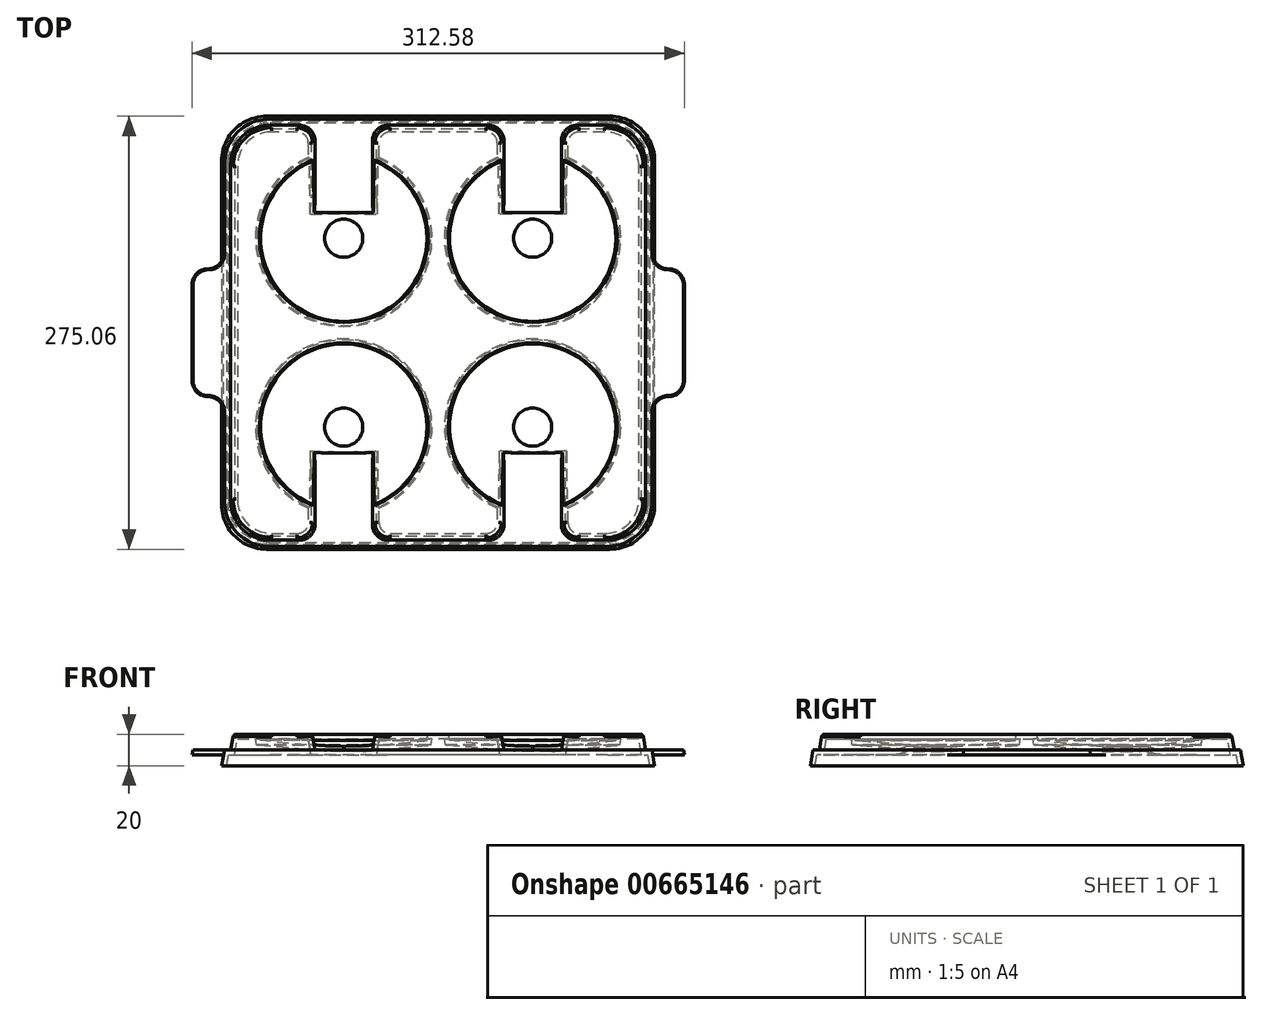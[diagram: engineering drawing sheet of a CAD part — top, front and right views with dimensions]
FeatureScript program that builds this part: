
annotation { "Feature Type Name" : "Feature", "Feature Type Description" : "" }
export const myFeature = defineFeature(function(context is Context, id is Id, definition is map)
    precondition{}
    {
        {
            var Q0;
            Q0=qCreatedBy(makeId("Top.planeOp"),FACE);
            var sketch = newSketch(context, id + "F0", { "sketchPlane" : qUnion([Q0])});
            skLineSegment(sketch, "E0", {"start": v(-60, 63.68) * mm, "end": v(-60, -68.5) * mm, "construction": true});
            skLineSegment(sketch, "E1", {"start": v(-108.87, 60) * mm, "end": v(91.95, 60) * mm, "construction": true});
            skLineSegment(sketch, "E2.MirrorCS", {"start": v(60, 63.68) * mm, "end": v(60, -68.5) * mm, "construction": true});
            skLineSegment(sketch, "E3.MirrorCS", {"start": v(-108.87, -60) * mm, "end": v(91.95, -60) * mm, "construction": true});
            skLineSegment(sketch, "E4", {"start": v(-130, 152.73) * mm, "end": v(-130, -156.18) * mm, "construction": true});
            skLineSegment(sketch, "E5", {"start": v(-201.2, -130) * mm, "end": v(310.8, -130) * mm, "construction": true});
            skLineSegment(sketch, "E6.MirrorCS", {"start": v(130, 152.73) * mm, "end": v(130, -156.18) * mm, "construction": true});
            skLineSegment(sketch, "E7.MirrorCS", {"start": v(-201.2, 130) * mm, "end": v(310.8, 130) * mm, "construction": true});
            skLineSegment(sketch, "E8.bottom", {"start": v(-130, 130) * mm, "end": v(130, 130) * mm});
            skLineSegment(sketch, "E8.top", {"start": v(-130, -130) * mm, "end": v(130, -130) * mm});
            skLineSegment(sketch, "E8.left", {"start": v(-130, 130) * mm, "end": v(-130, -130) * mm});
            skLineSegment(sketch, "E8.right", {"start": v(130, 130) * mm, "end": v(130, -130) * mm});
            skSolve(sketch);
        }
        {
            var Q0;
            Q0=makeQuery(id+"F0.imprint","IMPRINT",FACE,{"disambiguationData":[TD([[makeQuery(id+"F0.imprint","IMPRINT",EDGE,{"derivedFrom":sQuery(id+"F0.wireOp",EDGE,"E8.bottom")}),-1.0]])]});
            extrude(context, id + "F1", {"entities" : qUnion([Q0]), "oppositeDirection" : true, "depth" : 10 * mm, "offsetDistance" : 25 * mm, "hasDraft" : true, "draftAngle" : 10 * degree});
        }
        {
            var Q0;
            Q0=makeQuery(id+"F1.opExtrude","CAP_FACE",FACE,{"disambiguationData":[OSD([sQuery(id+"F0.wireOp",EDGE,"E8.bottom"),sQuery(id+"F0.wireOp",EDGE,"E8.top"),sQuery(id+"F0.wireOp",EDGE,"E8.left"),sQuery(id+"F0.wireOp",EDGE,"E8.right")])],"isStart":false});
            var sketch = newSketch(context, id + "F2", { "sketchPlane" : qUnion([Q0])});
            skLineSegment(sketch, "E9", {"start": v(-264, 135.76) * mm, "end": v(236, 135.76) * mm, "construction": true});
            skLineSegment(sketch, "E10.MirrorCS", {"start": v(-264, -135.76) * mm, "end": v(236, -135.76) * mm, "construction": true});
            skLineSegment(sketch, "E11", {"start": v(-135.76, 316.9) * mm, "end": v(-135.76, -183.1) * mm, "construction": true});
            skLineSegment(sketch, "E12.MirrorCS", {"start": v(135.76, 316.9) * mm, "end": v(135.76, -183.1) * mm, "construction": true});
            skLineSegment(sketch, "E13.bottom", {"start": v(-135.76, 135.76) * mm, "end": v(135.76, 135.76) * mm});
            skLineSegment(sketch, "E13.top", {"start": v(-135.76, -135.76) * mm, "end": v(135.76, -135.76) * mm});
            skLineSegment(sketch, "E13.left", {"start": v(-135.76, 135.76) * mm, "end": v(-135.76, -135.76) * mm});
            skLineSegment(sketch, "E13.right", {"start": v(135.76, 135.76) * mm, "end": v(135.76, -135.76) * mm});
            skSolve(sketch);
        }
        {
            var Q0;
            Q0=makeQuery(id+"F2.imprint","IMPRINT",FACE,{"disambiguationData":[TD([[makeQuery(id+"F2.imprint","IMPRINT",EDGE,{"derivedFrom":sQuery(id+"F2.wireOp",EDGE,"E13.bottom")}),-1.0]])]});
            var Q1;
            Q1=makeQuery(id+"F2.imprint","IMPRINT",FACE,{"disambiguationData":[TD([[makeQuery(id+"F2.imprint","IMPRINT",EDGE,{"derivedFrom":makeQuery(id+"F1.opExtrude","CAP_EDGE",EDGE,{"disambiguationData":[OSD([sQuery(id+"F0.wireOp",EDGE,"E8.bottom")])],"isStart":false})}),1.0]])]});
            extrude(context, id + "F3", {"entities" : qUnion([Q0, Q1]), "operationType" : NewBodyOperationType.ADD, "depth" : 10 * mm, "offsetDistance" : 25 * mm, "hasDraft" : true, "draftAngle" : 10 * degree});
        }
        {
            var Q0;
            Q0=makeQuery(id+"F1.opExtrude","CAP_FACE",FACE,{"disambiguationData":[OSD([sQuery(id+"F0.wireOp",EDGE,"E8.bottom"),sQuery(id+"F0.wireOp",EDGE,"E8.top"),sQuery(id+"F0.wireOp",EDGE,"E8.left"),sQuery(id+"F0.wireOp",EDGE,"E8.right")])],"isStart":true});
            var sketch = newSketch(context, id + "F4", { "sketchPlane" : qUnion([Q0])});
            skLineSegment(sketch, "E14", {"start": v(-130, 0) * mm, "end": v(130, 0) * mm, "construction": true});
            skLineSegment(sketch, "E15", {"start": v(-130, -60) * mm, "end": v(130, -60) * mm, "construction": true});
            skLineSegment(sketch, "E16.MirrorCS", {"start": v(-130, 60) * mm, "end": v(130, 60) * mm, "construction": true});
            skLineSegment(sketch, "E17", {"start": v(-60, -130) * mm, "end": v(-60, 130) * mm, "construction": true});
            skLineSegment(sketch, "E18", {"start": v(0, -130) * mm, "end": v(0, 130) * mm, "construction": true});
            skLineSegment(sketch, "E19.MirrorCS", {"start": v(60, -130) * mm, "end": v(60, 130) * mm, "construction": true});
            skCircle(sketch, "E20", {"center": v(-60, -60) * mm, "radius": 53.5 * mm});
            skCircle(sketch, "E21", {"center": v(-60, 60) * mm, "radius": 53.5 * mm});
            skCircle(sketch, "E22", {"center": v(60, 60) * mm, "radius": 53.5 * mm});
            skCircle(sketch, "E23", {"center": v(60, -60) * mm, "radius": 53.5 * mm});
            skCircle(sketch, "E24", {"center": v(60, 60) * mm, "radius": 25 * mm, "construction": true});
            skLineSegment(sketch, "E25", {"start": v(80, 150) * mm, "end": v(80, 75) * mm});
            skLineSegment(sketch, "E26.MirrorCS", {"start": v(40, 130) * mm, "end": v(40, 75) * mm});
            skLineSegment(sketch, "E27.MirrorCS", {"start": v(-40, 130) * mm, "end": v(-40, 75) * mm});
            skLineSegment(sketch, "E28.MirrorCS", {"start": v(-80, 130) * mm, "end": v(-80, 75) * mm});
            skCircle(sketch, "E29.MirrorC", {"center": v(-60, 60) * mm, "radius": 25 * mm, "construction": true});
            skCircle(sketch, "E30.MirrorC", {"center": v(60, -60) * mm, "radius": 25 * mm, "construction": true});
            skLineSegment(sketch, "E31.MirrorCS", {"start": v(40, -130) * mm, "end": v(40, -75) * mm});
            skLineSegment(sketch, "E32.MirrorCS", {"start": v(80, -130) * mm, "end": v(80, -75) * mm});
            skCircle(sketch, "E33.MirrorC", {"center": v(-60, -60) * mm, "radius": 25 * mm, "construction": true});
            skLineSegment(sketch, "E34.MirrorCS", {"start": v(-80, -130) * mm, "end": v(-80, -75) * mm});
            skLineSegment(sketch, "E35.MirrorCS", {"start": v(-40, -130) * mm, "end": v(-40, -75) * mm});
            skLineSegment(sketch, "E36", {"start": v(40, 75) * mm, "end": v(80, 75) * mm});
            skLineSegment(sketch, "E37.MirrorCS", {"start": v(-40, 75) * mm, "end": v(-80, 75) * mm});
            skLineSegment(sketch, "E38.MirrorCS", {"start": v(-40, -75) * mm, "end": v(-80, -75) * mm});
            skLineSegment(sketch, "E39.MirrorCS", {"start": v(40, -75) * mm, "end": v(80, -75) * mm});
            skPoint(sketch, "E40.orphan", {"position": v(80, 130) * mm});
            skLineSegment(sketch, "E41.MirrorCS", {"start": v(40, 150) * mm, "end": v(40, 75) * mm});
            skLineSegment(sketch, "E42.MirrorCS", {"start": v(-40, 150) * mm, "end": v(-40, 75) * mm});
            skLineSegment(sketch, "E43.MirrorCS", {"start": v(-80, 150) * mm, "end": v(-80, 75) * mm});
            skLineSegment(sketch, "E44.MirrorCS", {"start": v(-40, -150) * mm, "end": v(-40, -75) * mm});
            skLineSegment(sketch, "E45.MirrorCS", {"start": v(-80, -150) * mm, "end": v(-80, -75) * mm});
            skLineSegment(sketch, "E46.MirrorCS", {"start": v(40, -150) * mm, "end": v(40, -75) * mm});
            skLineSegment(sketch, "E47.MirrorCS", {"start": v(80, -150) * mm, "end": v(80, -75) * mm});
            skLineSegment(sketch, "E48", {"start": v(-80, 150) * mm, "end": v(-40, 150) * mm});
            skLineSegment(sketch, "E49", {"start": v(40, 150) * mm, "end": v(80, 150) * mm});
            skLineSegment(sketch, "E50", {"start": v(-80, -150) * mm, "end": v(-40, -150) * mm});
            skLineSegment(sketch, "E51", {"start": v(40, -150) * mm, "end": v(80, -150) * mm});
            skSolve(sketch);
        }
        {
            var Q0;
            {var subQ5=sQuery(id+"F4.wireOp",EDGE,"E39.MirrorCS");Q0=makeQuery(id+"F4.imprint","IMPRINT",FACE,{"disambiguationData":[TD([[makeQuery(id+"F4.imprint","IMPRINT",EDGE,{"derivedFrom":subQ5}),1.0]])]});}
            var Q1;
            {var subQ5=sQuery(id+"F4.wireOp",EDGE,"E39.MirrorCS");Q1=makeQuery(id+"F4.imprint","IMPRINT",FACE,{"disambiguationData":[TD([[makeQuery(id+"F4.imprint","IMPRINT",EDGE,{"derivedFrom":subQ5}),-1.0]])]});}
            var Q2;
            {var subQ5=sQuery(id+"F4.wireOp",EDGE,"E38.MirrorCS");Q2=makeQuery(id+"F4.imprint","IMPRINT",FACE,{"disambiguationData":[TD([[makeQuery(id+"F4.imprint","IMPRINT",EDGE,{"derivedFrom":subQ5}),1.0]])]});}
            var Q3;
            {var subQ5=sQuery(id+"F4.wireOp",EDGE,"E38.MirrorCS");Q3=makeQuery(id+"F4.imprint","IMPRINT",FACE,{"disambiguationData":[TD([[makeQuery(id+"F4.imprint","IMPRINT",EDGE,{"derivedFrom":subQ5}),-1.0]])]});}
            var Q4;
            {var subQ5=sQuery(id+"F4.wireOp",EDGE,"E37.MirrorCS");Q4=makeQuery(id+"F4.imprint","IMPRINT",FACE,{"disambiguationData":[TD([[makeQuery(id+"F4.imprint","IMPRINT",EDGE,{"derivedFrom":subQ5}),1.0]])]});}
            var Q5;
            {var subQ5=sQuery(id+"F4.wireOp",EDGE,"E37.MirrorCS");Q5=makeQuery(id+"F4.imprint","IMPRINT",FACE,{"disambiguationData":[TD([[makeQuery(id+"F4.imprint","IMPRINT",EDGE,{"derivedFrom":subQ5}),-1.0]])]});}
            var Q6;
            {var subQ5=sQuery(id+"F4.wireOp",EDGE,"E36");Q6=makeQuery(id+"F4.imprint","IMPRINT",FACE,{"disambiguationData":[TD([[makeQuery(id+"F4.imprint","IMPRINT",EDGE,{"derivedFrom":subQ5}),1.0]])]});}
            var Q7;
            {var subQ5=sQuery(id+"F4.wireOp",EDGE,"E36");Q7=makeQuery(id+"F4.imprint","IMPRINT",FACE,{"disambiguationData":[TD([[makeQuery(id+"F4.imprint","IMPRINT",EDGE,{"derivedFrom":subQ5}),-1.0]])]});}
            extrude(context, id + "F5", {"entities" : qUnion([Q0, Q1, Q2, Q3, Q4, Q5, Q6, Q7]), "operationType" : NewBodyOperationType.REMOVE, "oppositeDirection" : true, "depth" : 8 * mm, "offsetDistance" : 25 * mm, "hasDraft" : true, "draftAngle" : 10 * degree, "draftPullDirection" : true});
        }
        {
            var Q0;
            Q0=makeQuery(id+"F5.boolean.opBoolean","COPY",FACE,{"derivedFrom":makeQuery(id+"F5.opExtrude","CAP_FACE",FACE,{"disambiguationData":[OSD([sQuery(id+"F4.wireOp",EDGE,"E20")])],"isStart":false})});
            var Q1;
            Q1=makeQuery(id+"F5.boolean.opBoolean","COPY",EDGE,{"derivedFrom":makeQuery(id+"F5.opExtrude","CAP_EDGE",EDGE,{"disambiguationData":[OSD([sQuery(id+"F4.wireOp",EDGE,"E23")])],"isStart":false})});
            var Q2;
            Q2=makeQuery(id+"F5.boolean.opBoolean","COPY",EDGE,{"derivedFrom":makeQuery(id+"F5.opExtrude","CAP_EDGE",EDGE,{"disambiguationData":[OSD([sQuery(id+"F4.wireOp",EDGE,"E22")])],"isStart":false})});
            var Q3;
            Q3=makeQuery(id+"F5.boolean.opBoolean","COPY",EDGE,{"derivedFrom":makeQuery(id+"F5.opExtrude","CAP_EDGE",EDGE,{"disambiguationData":[OSD([sQuery(id+"F4.wireOp",EDGE,"E21")])],"isStart":false})});
            chamfer(context, id + "F6", {"entities" : qUnion([Q0, Q1, Q2, Q3]), "chamferType" : ChamferType.TWO_OFFSETS, "width1" : 40 * mm, "oppositeDirection" : false, "width2" : 4 * mm, "tangentPropagation" : true});
        }
        {
            var Q0;
            {var subQ5=sQuery(id+"F4.wireOp",EDGE,"E37.MirrorCS");Q0=makeQuery(id+"F4.imprint","IMPRINT",FACE,{"disambiguationData":[TD([[makeQuery(id+"F4.imprint","IMPRINT",EDGE,{"derivedFrom":subQ5}),-1.0]])]});}
            var Q1;
            {var subQ0=sQuery(id+"F4.wireOp",EDGE,"E27.MirrorCS");var subQ1=sQuery(id+"F4.wireOp",EDGE,"E21");var subQ2=makeQuery(id+"F4.imprint","INTERSECT",VERTEX,{"derivedFrom":[subQ1,subQ0]});Q1=makeQuery(id+"F4.imprint","IMPRINT",FACE,{"disambiguationData":[TD([[makeQuery(id+"F4.imprint","IMPRINT",EDGE,{"disambiguationData":[TD([[subQ2,-1.0]])],"derivedFrom":subQ1}),-1.0]])]});}
            var Q2;
            {var subQ0=sQuery(id+"F4.wireOp",EDGE,"E25");var subQ1=sQuery(id+"F4.wireOp",EDGE,"E22");var subQ2=makeQuery(id+"F4.imprint","INTERSECT",VERTEX,{"derivedFrom":[subQ1,subQ0]});Q2=makeQuery(id+"F4.imprint","IMPRINT",FACE,{"disambiguationData":[TD([[makeQuery(id+"F4.imprint","IMPRINT",EDGE,{"disambiguationData":[TD([[subQ2,-1.0]])],"derivedFrom":subQ1}),-1.0]])]});}
            var Q3;
            {var subQ5=sQuery(id+"F4.wireOp",EDGE,"E36");Q3=makeQuery(id+"F4.imprint","IMPRINT",FACE,{"disambiguationData":[TD([[makeQuery(id+"F4.imprint","IMPRINT",EDGE,{"derivedFrom":subQ5}),1.0]])]});}
            var Q4;
            {var subQ5=sQuery(id+"F4.wireOp",EDGE,"E38.MirrorCS");Q4=makeQuery(id+"F4.imprint","IMPRINT",FACE,{"disambiguationData":[TD([[makeQuery(id+"F4.imprint","IMPRINT",EDGE,{"derivedFrom":subQ5}),1.0]])]});}
            var Q5;
            {var subQ0=sQuery(id+"F4.wireOp",EDGE,"E34.MirrorCS");var subQ1=sQuery(id+"F4.wireOp",EDGE,"E20");var subQ2=makeQuery(id+"F4.imprint","INTERSECT",VERTEX,{"derivedFrom":[subQ1,subQ0]});Q5=makeQuery(id+"F4.imprint","IMPRINT",FACE,{"disambiguationData":[TD([[makeQuery(id+"F4.imprint","IMPRINT",EDGE,{"disambiguationData":[TD([[subQ2,-1.0]])],"derivedFrom":subQ1}),-1.0]])]});}
            var Q6;
            {var subQ0=sQuery(id+"F4.wireOp",EDGE,"E31.MirrorCS");var subQ1=sQuery(id+"F4.wireOp",EDGE,"E23");var subQ2=makeQuery(id+"F4.imprint","INTERSECT",VERTEX,{"derivedFrom":[subQ1,subQ0]});Q6=makeQuery(id+"F4.imprint","IMPRINT",FACE,{"disambiguationData":[TD([[makeQuery(id+"F4.imprint","IMPRINT",EDGE,{"disambiguationData":[TD([[subQ2,-1.0]])],"derivedFrom":subQ1}),-1.0]])]});}
            var Q7;
            {var subQ5=sQuery(id+"F4.wireOp",EDGE,"E39.MirrorCS");Q7=makeQuery(id+"F4.imprint","IMPRINT",FACE,{"disambiguationData":[TD([[makeQuery(id+"F4.imprint","IMPRINT",EDGE,{"derivedFrom":subQ5}),-1.0]])]});}
            var Q8;
            {var subQ0=sQuery(id+"F4.wireOp",EDGE,"E49");Q8=makeQuery(id+"F4.imprint","IMPRINT",FACE,{"disambiguationData":[TD([[makeQuery(id+"F4.imprint","IMPRINT",EDGE,{"derivedFrom":subQ0}),-1.0]])]});}
            var Q9;
            {var subQ0=sQuery(id+"F4.wireOp",EDGE,"E48");Q9=makeQuery(id+"F4.imprint","IMPRINT",FACE,{"disambiguationData":[TD([[makeQuery(id+"F4.imprint","IMPRINT",EDGE,{"derivedFrom":subQ0}),-1.0]])]});}
            var Q10;
            {var subQ0=sQuery(id+"F4.wireOp",EDGE,"E51");Q10=makeQuery(id+"F4.imprint","IMPRINT",FACE,{"disambiguationData":[TD([[makeQuery(id+"F4.imprint","IMPRINT",EDGE,{"derivedFrom":subQ0}),1.0]])]});}
            var Q11;
            {var subQ0=sQuery(id+"F4.wireOp",EDGE,"E50");Q11=makeQuery(id+"F4.imprint","IMPRINT",FACE,{"disambiguationData":[TD([[makeQuery(id+"F4.imprint","IMPRINT",EDGE,{"derivedFrom":subQ0}),1.0]])]});}
            extrude(context, id + "F7", {"entities" : qUnion([Q0, Q1, Q2, Q3, Q4, Q5, Q6, Q7, Q8, Q9, Q10, Q11]), "operationType" : NewBodyOperationType.REMOVE, "oppositeDirection" : true, "depth" : 10 * mm, "offsetDistance" : 25 * mm, "hasDraft" : true, "draftAngle" : 10 * degree, "draftPullDirection" : true});
        }
        {
            var Q0;
            Q0=makeQuery(id+"F7.boolean.opBoolean","COPY",EDGE,{"derivedFrom":makeQuery(id+"F7.opExtrude","CAP_EDGE",EDGE,{"disambiguationData":[OSD([sQuery(id+"F4.wireOp",EDGE,"E39.MirrorCS")])],"isStart":false})});
            var Q1;
            Q1=makeQuery(id+"F7.boolean.opBoolean","COPY",EDGE,{"derivedFrom":makeQuery(id+"F7.opExtrude","CAP_EDGE",EDGE,{"disambiguationData":[OSD([sQuery(id+"F4.wireOp",EDGE,"E38.MirrorCS")])],"isStart":false})});
            var Q2;
            Q2=makeQuery(id+"F7.boolean.opBoolean","COPY",EDGE,{"derivedFrom":makeQuery(id+"F7.opExtrude","CAP_EDGE",EDGE,{"disambiguationData":[OSD([sQuery(id+"F4.wireOp",EDGE,"E37.MirrorCS")])],"isStart":false})});
            var Q3;
            Q3=makeQuery(id+"F7.boolean.opBoolean","COPY",EDGE,{"derivedFrom":makeQuery(id+"F7.opExtrude","CAP_EDGE",EDGE,{"disambiguationData":[OSD([sQuery(id+"F4.wireOp",EDGE,"E36")])],"isStart":false})});
            fillet(context, id + "F8", {"entities" : qUnion([Q0, Q1, Q2, Q3]), "radius" : 15 * mm, "tangentPropagation" : true, "allowEdgeOverflow" : false});
        }
        {
            var Q0;
            Q0=makeQuery(id+"F7.boolean.opBoolean","INTERSECT",EDGE,{"derivedFrom":[makeQuery(id+"F1.opExtrude","SWEPT_FACE",FACE,{"disambiguationData":[OSD([sQuery(id+"F0.wireOp",EDGE,"E8.bottom")])]}),makeQuery(id+"F7.opExtrude","SWEPT_FACE",FACE,{"disambiguationData":[OSD([sQuery(id+"F4.wireOp",EDGE,"E42.MirrorCS")])]})]});
            var Q1;
            Q1=makeQuery(id+"F7.boolean.opBoolean","INTERSECT",EDGE,{"derivedFrom":[makeQuery(id+"F1.opExtrude","SWEPT_FACE",FACE,{"disambiguationData":[OSD([sQuery(id+"F0.wireOp",EDGE,"E8.bottom")])]}),makeQuery(id+"F7.opExtrude","SWEPT_FACE",FACE,{"disambiguationData":[OSD([sQuery(id+"F4.wireOp",EDGE,"E25")])]})]});
            var Q2;
            Q2=makeQuery(id+"F7.boolean.opBoolean","INTERSECT",EDGE,{"derivedFrom":[makeQuery(id+"F1.opExtrude","SWEPT_FACE",FACE,{"disambiguationData":[OSD([sQuery(id+"F0.wireOp",EDGE,"E8.bottom")])]}),makeQuery(id+"F7.opExtrude","SWEPT_FACE",FACE,{"disambiguationData":[OSD([sQuery(id+"F4.wireOp",EDGE,"E41.MirrorCS")])]})]});
            var Q3;
            Q3=makeQuery(id+"F7.boolean.opBoolean","INTERSECT",EDGE,{"derivedFrom":[makeQuery(id+"F1.opExtrude","SWEPT_FACE",FACE,{"disambiguationData":[OSD([sQuery(id+"F0.wireOp",EDGE,"E8.bottom")])]}),makeQuery(id+"F7.opExtrude","SWEPT_FACE",FACE,{"disambiguationData":[OSD([sQuery(id+"F4.wireOp",EDGE,"E43.MirrorCS")])]})]});
            var Q4;
            Q4=makeQuery(id+"F7.boolean.opBoolean","INTERSECT",EDGE,{"derivedFrom":[makeQuery(id+"F1.opExtrude","SWEPT_FACE",FACE,{"disambiguationData":[OSD([sQuery(id+"F0.wireOp",EDGE,"E8.top")])]}),makeQuery(id+"F7.opExtrude","SWEPT_FACE",FACE,{"disambiguationData":[OSD([sQuery(id+"F4.wireOp",EDGE,"E45.MirrorCS")])]})]});
            var Q5;
            Q5=makeQuery(id+"F7.boolean.opBoolean","INTERSECT",EDGE,{"derivedFrom":[makeQuery(id+"F1.opExtrude","SWEPT_FACE",FACE,{"disambiguationData":[OSD([sQuery(id+"F0.wireOp",EDGE,"E8.top")])]}),makeQuery(id+"F7.opExtrude","SWEPT_FACE",FACE,{"disambiguationData":[OSD([sQuery(id+"F4.wireOp",EDGE,"E44.MirrorCS")])]})]});
            var Q6;
            Q6=makeQuery(id+"F7.boolean.opBoolean","INTERSECT",EDGE,{"derivedFrom":[makeQuery(id+"F1.opExtrude","SWEPT_FACE",FACE,{"disambiguationData":[OSD([sQuery(id+"F0.wireOp",EDGE,"E8.top")])]}),makeQuery(id+"F7.opExtrude","SWEPT_FACE",FACE,{"disambiguationData":[OSD([sQuery(id+"F4.wireOp",EDGE,"E47.MirrorCS")])]})]});
            var Q7;
            Q7=makeQuery(id+"F7.boolean.opBoolean","INTERSECT",EDGE,{"derivedFrom":[makeQuery(id+"F1.opExtrude","SWEPT_FACE",FACE,{"disambiguationData":[OSD([sQuery(id+"F0.wireOp",EDGE,"E8.top")])]}),makeQuery(id+"F7.opExtrude","SWEPT_FACE",FACE,{"disambiguationData":[OSD([sQuery(id+"F4.wireOp",EDGE,"E46.MirrorCS")])]})]});
            fillet(context, id + "F9", {"entities" : qUnion([Q0, Q1, Q2, Q3, Q4, Q5, Q6, Q7]), "radius" : 10 * mm, "tangentPropagation" : true, "allowEdgeOverflow" : false});
        }
        {
            var Q0;
            Q0=makeQuery(id+"F1.opExtrude","SWEPT_EDGE",EDGE,{"disambiguationData":[OSD([sQuery(id+"F0.wireOp",EDGE,"E8.top"),sQuery(id+"F0.wireOp",EDGE,"E8.left")])]});
            var Q1;
            Q1=makeQuery(id+"F1.opExtrude","SWEPT_EDGE",EDGE,{"disambiguationData":[OSD([sQuery(id+"F0.wireOp",EDGE,"E8.top"),sQuery(id+"F0.wireOp",EDGE,"E8.right")])]});
            var Q2;
            Q2=makeQuery(id+"F1.opExtrude","SWEPT_EDGE",EDGE,{"disambiguationData":[OSD([sQuery(id+"F0.wireOp",EDGE,"E8.bottom"),sQuery(id+"F0.wireOp",EDGE,"E8.right")])]});
            var Q3;
            Q3=makeQuery(id+"F1.opExtrude","SWEPT_EDGE",EDGE,{"disambiguationData":[OSD([sQuery(id+"F0.wireOp",EDGE,"E8.bottom"),sQuery(id+"F0.wireOp",EDGE,"E8.left")])]});
            fillet(context, id + "F10", {"entities" : qUnion([Q0, Q1, Q2, Q3]), "radius" : 25 * mm, "tangentPropagation" : true, "allowEdgeOverflow" : false});
        }
        {
            var Q0;
            Q0=makeQuery(id+"F3.opExtrude","SWEPT_EDGE",EDGE,{"disambiguationData":[OSD([sQuery(id+"F2.wireOp",EDGE,"E13.bottom"),sQuery(id+"F2.wireOp",EDGE,"E13.right")])]});
            var Q1;
            Q1=makeQuery(id+"F3.opExtrude","SWEPT_EDGE",EDGE,{"disambiguationData":[OSD([sQuery(id+"F2.wireOp",EDGE,"E13.top"),sQuery(id+"F2.wireOp",EDGE,"E13.right")])]});
            var Q2;
            Q2=makeQuery(id+"F3.opExtrude","SWEPT_EDGE",EDGE,{"disambiguationData":[OSD([sQuery(id+"F2.wireOp",EDGE,"E13.top"),sQuery(id+"F2.wireOp",EDGE,"E13.left")])]});
            var Q3;
            Q3=makeQuery(id+"F3.opExtrude","SWEPT_EDGE",EDGE,{"disambiguationData":[OSD([sQuery(id+"F2.wireOp",EDGE,"E13.bottom"),sQuery(id+"F2.wireOp",EDGE,"E13.left")])]});
            fillet(context, id + "F11", {"entities" : qUnion([Q0, Q1, Q2, Q3]), "radius" : 29 * mm, "tangentPropagation" : true, "allowEdgeOverflow" : false});
        }
        {
            var Q0;
            Q0=makeQuery(id+"F3.opExtrude","CAP_FACE",FACE,{"disambiguationData":[OSD([sQuery(id+"F2.wireOp",EDGE,"E13.bottom"),sQuery(id+"F2.wireOp",EDGE,"E13.top"),sQuery(id+"F2.wireOp",EDGE,"E13.left"),sQuery(id+"F2.wireOp",EDGE,"E13.right")])],"isStart":false});
            shell(context, id + "F12", {"entities" : qUnion([Q0]), "thickness" : 3 * mm});
        }
        {
            var Q0;
            Q0=makeQuery(id+"F1.opExtrude","CAP_EDGE",EDGE,{"disambiguationData":[OSD([sQuery(id+"F0.wireOp",EDGE,"E8.right")])],"isStart":true});
            var Q1;
            {var subQ0=sQuery(id+"F0.wireOp",EDGE,"E8.bottom");Q1=makeQuery(id+"F7.boolean.opBoolean","SPLIT",EDGE,{"disambiguationData":[TD([makeQuery(id+"F7.opExtrude","SWEPT_FACE",FACE,{"disambiguationData":[OSD([sQuery(id+"F4.wireOp",EDGE,"E41.MirrorCS")])]})])],"derivedFrom":makeQuery(id+"F1.opExtrude","CAP_EDGE",EDGE,{"disambiguationData":[OSD([subQ0])],"isStart":true})});}
            var Q2;
            Q2=makeQuery(id+"F1.opExtrude","CAP_EDGE",EDGE,{"disambiguationData":[OSD([sQuery(id+"F0.wireOp",EDGE,"E8.left")])],"isStart":true});
            var Q3;
            {var subQ0=sQuery(id+"F0.wireOp",EDGE,"E8.top");Q3=makeQuery(id+"F7.boolean.opBoolean","SPLIT",EDGE,{"disambiguationData":[TD([makeQuery(id+"F7.opExtrude","SWEPT_FACE",FACE,{"disambiguationData":[OSD([sQuery(id+"F4.wireOp",EDGE,"E44.MirrorCS")])]})])],"derivedFrom":makeQuery(id+"F1.opExtrude","CAP_EDGE",EDGE,{"disambiguationData":[OSD([subQ0])],"isStart":true})});}
            fillet(context, id + "F13", {"entities" : qUnion([Q0, Q1, Q2, Q3]), "radius" : 2 * mm, "tangentPropagation" : true, "allowEdgeOverflow" : false});
        }
        {
            var Q0;
            Q0=makeQuery(id+"F7.boolean.opBoolean","MERGE",FACE,{"derivedFrom":[makeQuery(id+"F3.opExtrude","CAP_FACE",FACE,{"disambiguationData":[OSD([sQuery(id+"F2.wireOp",EDGE,"E13.bottom"),sQuery(id+"F2.wireOp",EDGE,"E13.top"),sQuery(id+"F2.wireOp",EDGE,"E13.left"),sQuery(id+"F2.wireOp",EDGE,"E13.right")])],"isStart":true}),makeQuery(id+"F7.opExtrude","CAP_FACE",FACE,{"disambiguationData":[OSD([sQuery(id+"F4.wireOp",EDGE,"E25"),sQuery(id+"F4.wireOp",EDGE,"E36"),sQuery(id+"F4.wireOp",EDGE,"E41.MirrorCS"),sQuery(id+"F4.wireOp",EDGE,"E49")])],"isStart":false}),makeQuery(id+"F7.opExtrude","CAP_FACE",FACE,{"disambiguationData":[OSD([sQuery(id+"F4.wireOp",EDGE,"E37.MirrorCS"),sQuery(id+"F4.wireOp",EDGE,"E42.MirrorCS"),sQuery(id+"F4.wireOp",EDGE,"E43.MirrorCS"),sQuery(id+"F4.wireOp",EDGE,"E48")])],"isStart":false}),makeQuery(id+"F7.opExtrude","CAP_FACE",FACE,{"disambiguationData":[OSD([sQuery(id+"F4.wireOp",EDGE,"E38.MirrorCS"),sQuery(id+"F4.wireOp",EDGE,"E44.MirrorCS"),sQuery(id+"F4.wireOp",EDGE,"E45.MirrorCS"),sQuery(id+"F4.wireOp",EDGE,"E50")])],"isStart":false}),makeQuery(id+"F7.opExtrude","CAP_FACE",FACE,{"disambiguationData":[OSD([sQuery(id+"F4.wireOp",EDGE,"E39.MirrorCS"),sQuery(id+"F4.wireOp",EDGE,"E46.MirrorCS"),sQuery(id+"F4.wireOp",EDGE,"E47.MirrorCS"),sQuery(id+"F4.wireOp",EDGE,"E51")])],"isStart":false})]});
            var sketch = newSketch(context, id + "F14", { "sketchPlane" : qUnion([Q0])});
            skLineSegment(sketch, "E52", {"start": v(-135.76, 0) * mm, "end": v(-209.56, 0) * mm, "construction": true});
            skLineSegment(sketch, "E53", {"start": v(-135.76, 40) * mm, "end": v(-155.76, 40) * mm});
            skLineSegment(sketch, "E54.MirrorCS", {"start": v(-135.76, -40) * mm, "end": v(-155.76, -40) * mm});
            skLineSegment(sketch, "E55", {"start": v(-155.76, 40) * mm, "end": v(-155.76, -40) * mm});
            skLineSegment(sketch, "E56.MirrorCS", {"start": v(155.76, 40) * mm, "end": v(155.76, -40) * mm});
            skLineSegment(sketch, "E57.MirrorCS", {"start": v(135.76, 40) * mm, "end": v(155.76, 40) * mm});
            skLineSegment(sketch, "E58.MirrorCS", {"start": v(135.76, -40) * mm, "end": v(155.76, -40) * mm});
            skSolve(sketch);
        }
        {
            var Q0;
            {var subQ0=sQuery(id+"F14.wireOp",EDGE,"E53");Q0=makeQuery(id+"F14.imprint","IMPRINT",FACE,{"disambiguationData":[TD([[makeQuery(id+"F14.imprint","IMPRINT",EDGE,{"derivedFrom":subQ0}),1.0]])]});}
            var Q1;
            Q1=makeQuery(id+"F14.imprint","IMPRINT",FACE,{"disambiguationData":[TD([[makeQuery(id+"F14.imprint","IMPRINT",EDGE,{"derivedFrom":sQuery(id+"F14.wireOp",EDGE,"E56.MirrorCS")}),-1.0]])]});
            extrude(context, id + "F15", {"entities" : qUnion([Q0, Q1]), "operationType" : NewBodyOperationType.ADD, "oppositeDirection" : true, "depth" : 3 * mm, "offsetDistance" : 25 * mm, "hasDraft" : true, "draftAngle" : 10 * degree});
        }
        {
            var Q0;
            Q0=makeQuery(id+"F15.boolean.opBoolean","INTERSECT",EDGE,{"derivedFrom":[makeQuery(id+"F3.opExtrude","SWEPT_FACE",FACE,{"disambiguationData":[OSD([sQuery(id+"F2.wireOp",EDGE,"E13.left")])]}),makeQuery(id+"F15.opExtrude","SWEPT_FACE",FACE,{"disambiguationData":[OSD([sQuery(id+"F14.wireOp",EDGE,"E54.MirrorCS")])]})]});
            var Q1;
            Q1=makeQuery(id+"F15.boolean.opBoolean","INTERSECT",EDGE,{"derivedFrom":[makeQuery(id+"F3.opExtrude","SWEPT_FACE",FACE,{"disambiguationData":[OSD([sQuery(id+"F2.wireOp",EDGE,"E13.left")])]}),makeQuery(id+"F15.opExtrude","SWEPT_FACE",FACE,{"disambiguationData":[OSD([sQuery(id+"F14.wireOp",EDGE,"E53")])]})]});
            var Q2;
            Q2=makeQuery(id+"F15.opExtrude","SWEPT_EDGE",EDGE,{"disambiguationData":[OSD([sQuery(id+"F14.wireOp",EDGE,"E53"),sQuery(id+"F14.wireOp",EDGE,"E55")])]});
            var Q3;
            Q3=makeQuery(id+"F15.opExtrude","SWEPT_EDGE",EDGE,{"disambiguationData":[OSD([sQuery(id+"F14.wireOp",EDGE,"E54.MirrorCS"),sQuery(id+"F14.wireOp",EDGE,"E55")])]});
            var Q4;
            Q4=makeQuery(id+"F15.opExtrude","SWEPT_EDGE",EDGE,{"disambiguationData":[OSD([sQuery(id+"F14.wireOp",EDGE,"E56.MirrorCS"),sQuery(id+"F14.wireOp",EDGE,"E58.MirrorCS")])]});
            var Q5;
            Q5=makeQuery(id+"F15.boolean.opBoolean","INTERSECT",EDGE,{"derivedFrom":[makeQuery(id+"F3.opExtrude","SWEPT_FACE",FACE,{"disambiguationData":[OSD([sQuery(id+"F2.wireOp",EDGE,"E13.right")])]}),makeQuery(id+"F15.opExtrude","SWEPT_FACE",FACE,{"disambiguationData":[OSD([sQuery(id+"F14.wireOp",EDGE,"E58.MirrorCS")])]})]});
            var Q6;
            Q6=makeQuery(id+"F15.boolean.opBoolean","INTERSECT",EDGE,{"derivedFrom":[makeQuery(id+"F3.opExtrude","SWEPT_FACE",FACE,{"disambiguationData":[OSD([sQuery(id+"F2.wireOp",EDGE,"E13.right")])]}),makeQuery(id+"F15.opExtrude","SWEPT_FACE",FACE,{"disambiguationData":[OSD([sQuery(id+"F14.wireOp",EDGE,"E57.MirrorCS")])]})]});
            var Q7;
            Q7=makeQuery(id+"F15.opExtrude","SWEPT_EDGE",EDGE,{"disambiguationData":[OSD([sQuery(id+"F14.wireOp",EDGE,"E56.MirrorCS"),sQuery(id+"F14.wireOp",EDGE,"E57.MirrorCS")])]});
            fillet(context, id + "F16", {"entities" : qUnion([Q0, Q1, Q2, Q3, Q4, Q5, Q6, Q7]), "radius" : 10 * mm, "tangentPropagation" : true, "allowEdgeOverflow" : false});
        }
    });
